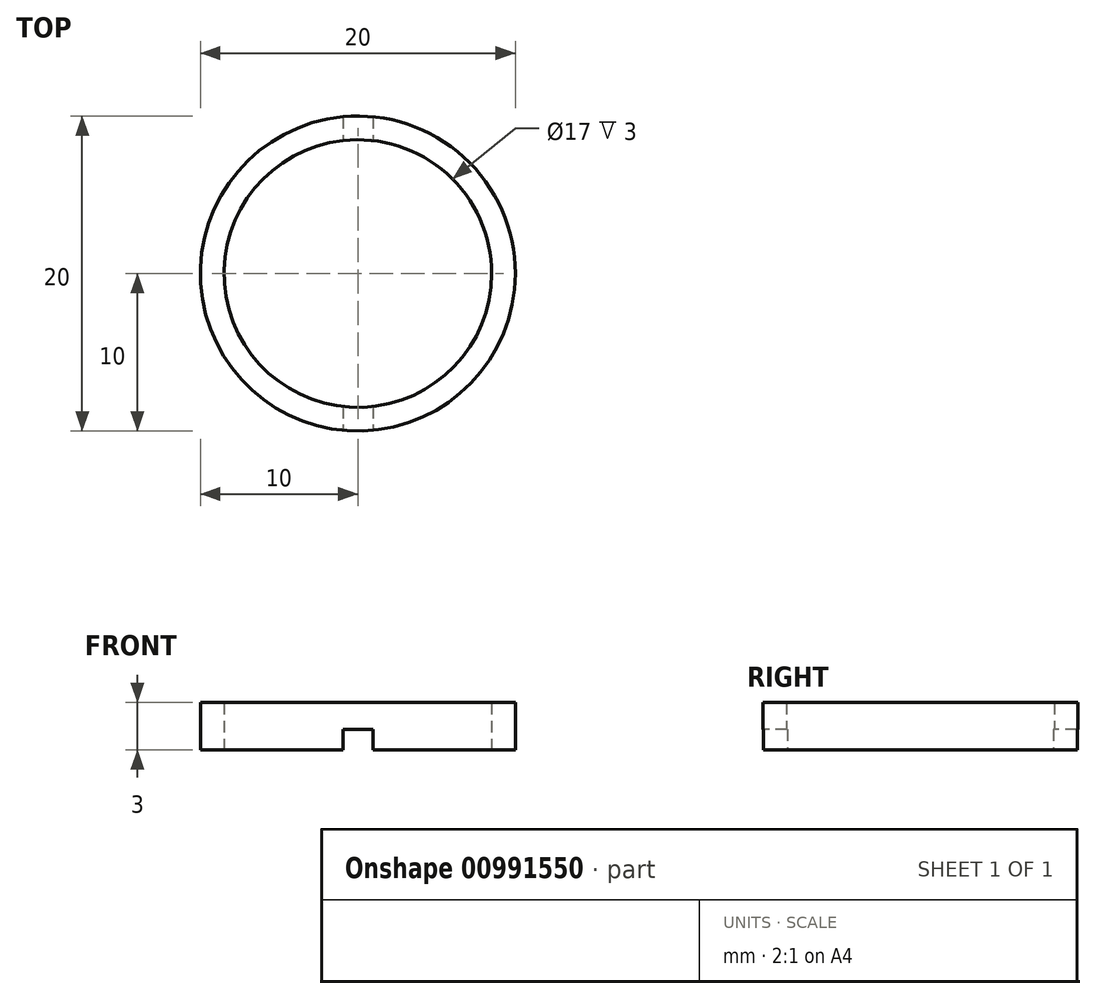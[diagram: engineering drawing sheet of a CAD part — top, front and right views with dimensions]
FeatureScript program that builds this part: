
annotation { "Feature Type Name" : "Feature", "Feature Type Description" : "" }
export const myFeature = defineFeature(function(context is Context, id is Id, definition is map)
    precondition{}
    {
        {
            var Q0;
            Q0=qCreatedBy(makeId("Top.planeOp"),FACE);
            var sketch = newSketch(context, id + "F0", { "sketchPlane" : qUnion([Q0])});
            skCircle(sketch, "E0", {"center": v(0, 0) * mm, "radius": 10 * mm});
            skCircle(sketch, "E1", {"center": v(0, 0) * mm, "radius": 8.5 * mm});
            skSolve(sketch);
        }
        {
            var Q0;
            Q0=makeQuery(id+"F0.imprint","IMPRINT",FACE,{"disambiguationData":[TD([[makeQuery(id+"F0.imprint","IMPRINT",EDGE,{"derivedFrom":sQuery(id+"F0.wireOp",EDGE,"E0")}),1.0]])]});
            extrude(context, id + "F1", {"entities" : qUnion([Q0]), "depth" : 3 * mm, "offsetDistance" : 25 * mm});
        }
        {
            var Q0;
            Q0=makeQuery(id+"F1.opExtrude","CAP_FACE",FACE,{"disambiguationData":[OSD([sQuery(id+"F0.wireOp",EDGE,"E0"),sQuery(id+"F0.wireOp",EDGE,"E1")])],"isStart":true});
            var sketch = newSketch(context, id + "F2", { "sketchPlane" : qUnion([Q0])});
            skLineSegment(sketch, "E2.bottom", {"start": v(0.95, -12.5) * mm, "end": v(-0.95, -12.5) * mm});
            skLineSegment(sketch, "E2.top", {"start": v(0.95, 12.5) * mm, "end": v(-0.95, 12.5) * mm});
            skLineSegment(sketch, "E2.left", {"start": v(0.95, -12.5) * mm, "end": v(0.95, 12.5) * mm});
            skLineSegment(sketch, "E2.right", {"start": v(-0.95, -12.5) * mm, "end": v(-0.95, 12.5) * mm});
            skSolve(sketch);
        }
        {
            var Q0;
            {var subQ0=sQuery(id+"F2.wireOp",EDGE,"E2.left");var subQ1=makeQuery(id+"F1.opExtrude","CAP_EDGE",EDGE,{"disambiguationData":[OSD([sQuery(id+"F0.wireOp",EDGE,"E0")])],"isStart":true});var subQ2=makeQuery(id+"F2.imprint","INTERSECT",VERTEX,{"disambiguationData":[OD(0.0)],"derivedFrom":[subQ1,subQ0]});Q0=makeQuery(id+"F2.imprint","IMPRINT",FACE,{"disambiguationData":[TD([[makeQuery(id+"F2.imprint","IMPRINT",EDGE,{"disambiguationData":[TD([[subQ2,-1.0]])],"derivedFrom":subQ0}),1.0]])]});}
            var Q1;
            {var subQ0=sQuery(id+"F2.wireOp",EDGE,"E2.left");var subQ1=makeQuery(id+"F1.opExtrude","CAP_EDGE",EDGE,{"disambiguationData":[OSD([sQuery(id+"F0.wireOp",EDGE,"E0")])],"isStart":true});var subQ2=makeQuery(id+"F2.imprint","INTERSECT",VERTEX,{"disambiguationData":[OD(1.0)],"derivedFrom":[subQ1,subQ0]});Q1=makeQuery(id+"F2.imprint","IMPRINT",FACE,{"disambiguationData":[TD([[makeQuery(id+"F2.imprint","IMPRINT",EDGE,{"disambiguationData":[TD([[subQ2,1.0]])],"derivedFrom":subQ0}),1.0]])]});}
            extrude(context, id + "F3", {"entities" : qUnion([Q0, Q1]), "operationType" : NewBodyOperationType.REMOVE, "oppositeDirection" : true, "depth" : 1.3 * mm, "offsetDistance" : 25 * mm});
        }
    });
